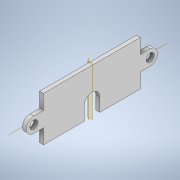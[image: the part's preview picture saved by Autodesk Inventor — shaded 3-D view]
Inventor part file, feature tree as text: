
AUTODESK INVENTOR PART (.ipt)
format: ipt  version: 2021 (Build 250183000, 183)  size: 136,192 bytes
history: native  units: mm
features: extrude x1, mirror x1, sketch x1
ambient origin geometry x8: Origin, YZ Plane, XZ Plane, XY Plane, X Axis, Y Axis, Z Axis, Center Point
bodies: Solid1 (feature_tree)
feature tree (3):
  extrude  "Extrusion1"  Depth=23.0mm
  mirror  "Mirror1"
  sketch  "Sketch1"  dims[d0=50.0mm d1=23.0mm d2=2.0mm d3=0.0mm d4=7.75mm d5=5.0mm d6=4.2mm d11=8.0mm d12=7.0mm]
